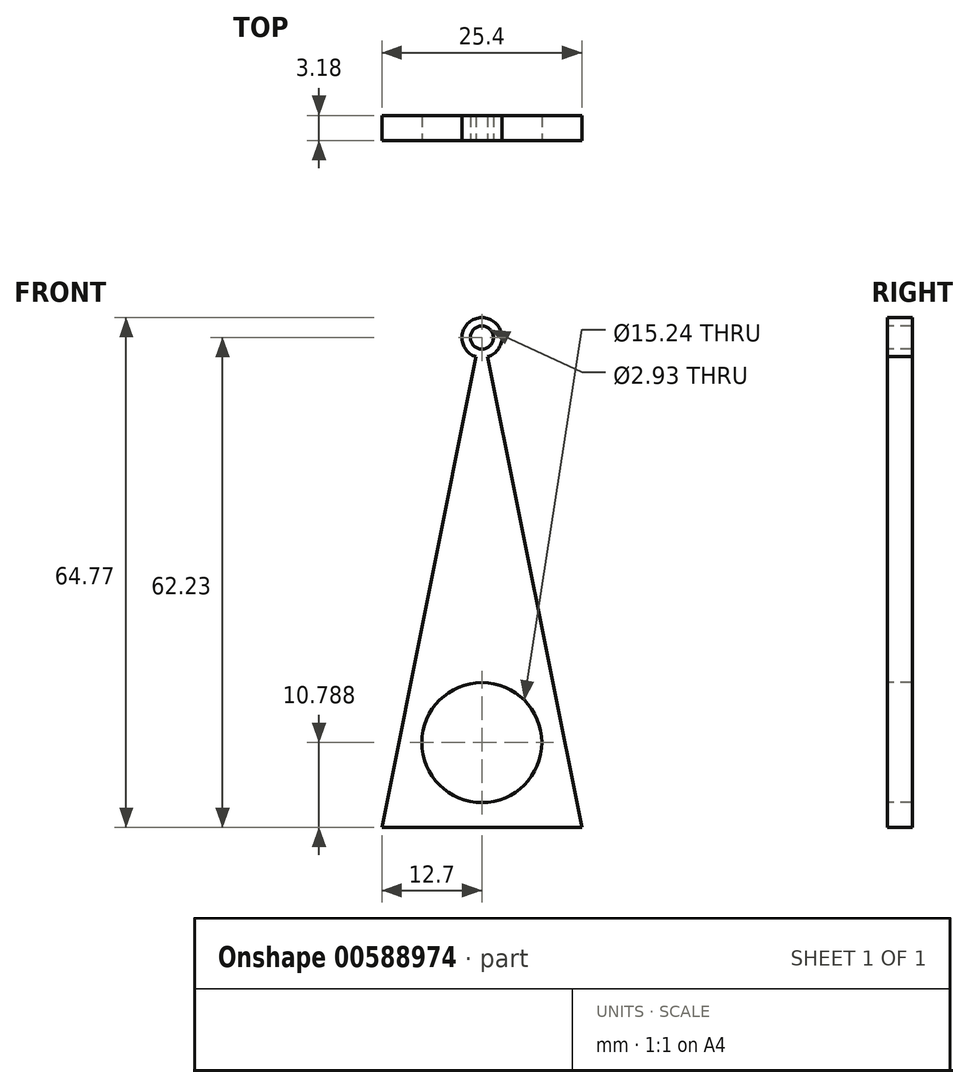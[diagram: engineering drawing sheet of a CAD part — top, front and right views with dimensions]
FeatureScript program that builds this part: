
annotation { "Feature Type Name" : "Feature", "Feature Type Description" : "" }
export const myFeature = defineFeature(function(context is Context, id is Id, definition is map)
    precondition{}
    {
        {
            var Q0;
            Q0=qCreatedBy(makeId("Front.planeOp"),FACE);
            var sketch = newSketch(context, id + "F0", { "sketchPlane" : qUnion([Q0])});
            skPoint(sketch, "E0", {"position": v(0, 38.1) * mm});
            skPoint(sketch, "E1", {"position": v(-12.7, -25.4) * mm});
            skPoint(sketch, "E2", {"position": v(12.7, -25.4) * mm});
            skLineSegment(sketch, "E3", {"start": v(0, 38.1) * mm, "end": v(-12.7, -25.4) * mm});
            skLineSegment(sketch, "E4", {"start": v(12.7, -25.4) * mm, "end": v(0, 38.1) * mm});
            skLineSegment(sketch, "E5", {"start": v(-12.7, -25.4) * mm, "end": v(12.7, -25.4) * mm});
            skSolve(sketch);
        }
        {
            var Q0;
            Q0 = qSketchRegion(id + "F0", true);
            extrude(context, id + "F1", {"entities" : qUnion([Q0]), "depth" : 3.17 * mm, "offsetDistance" : 25.4 * mm});
        }
        {
            var Q0;
            Q0=makeQuery(id+"F1.opExtrude","CAP_FACE",FACE,{"disambiguationData":[OSD([sQuery(id+"F0.wireOp",EDGE,"E3"),sQuery(id+"F0.wireOp",EDGE,"E4"),sQuery(id+"F0.wireOp",EDGE,"E5")])],"isStart":false});
            var sketch = newSketch(context, id + "F2", { "sketchPlane" : qUnion([Q0])});
            skCircle(sketch, "E6", {"center": v(0, -14.61) * mm, "radius": 7.62 * mm});
            skSolve(sketch);
        }
        {
            var Q0;
            Q0=makeQuery(id+"F2.imprint","IMPRINT",FACE,{"disambiguationData":[TD([[makeQuery(id+"F2.imprint","IMPRINT",EDGE,{"derivedFrom":sQuery(id+"F2.wireOp",EDGE,"E6")}),1.0]])]});
            extrude(context, id + "F3", {"entities" : qUnion([Q0]), "operationType" : NewBodyOperationType.REMOVE, "endBound" : BoundingType.THROUGH_ALL, "oppositeDirection" : true, "depth" : 25.4 * mm, "offsetDistance" : 25.4 * mm});
        }
        {
            var Q0;
            Q0=makeQuery(id+"F1.opExtrude","CAP_FACE",FACE,{"disambiguationData":[OSD([sQuery(id+"F0.wireOp",EDGE,"E3"),sQuery(id+"F0.wireOp",EDGE,"E4"),sQuery(id+"F0.wireOp",EDGE,"E5")])],"isStart":false});
            var sketch = newSketch(context, id + "F4", { "sketchPlane" : qUnion([Q0])});
            skCircle(sketch, "E7", {"center": v(0, 36.83) * mm, "radius": 2.54 * mm});
            skSolve(sketch);
        }
        {
            var Q0;
            {var subQ0=sQuery(id+"F4.wireOp",EDGE,"E7");var subQ1=makeQuery(id+"F1.opExtrude","CAP_EDGE",EDGE,{"disambiguationData":[OSD([sQuery(id+"F0.wireOp",EDGE,"E3")])],"isStart":false});var subQ2=makeQuery(id+"F4.imprint","INTERSECT",VERTEX,{"derivedFrom":[subQ1,subQ0]});Q0=makeQuery(id+"F4.imprint","IMPRINT",FACE,{"disambiguationData":[TD([[makeQuery(id+"F4.imprint","IMPRINT",EDGE,{"disambiguationData":[TD([[subQ2,1.0]])],"derivedFrom":subQ0}),1.0]])]});}
            var Q1;
            Q1=sQuery(id+"F4.wireOp",EDGE,"E7");
            var Q2;
            Q2=makeQuery(id+"F1.opExtrude","CAP_FACE",FACE,{"disambiguationData":[OSD([sQuery(id+"F0.wireOp",EDGE,"E3"),sQuery(id+"F0.wireOp",EDGE,"E4"),sQuery(id+"F0.wireOp",EDGE,"E5")])],"isStart":true});
            extrude(context, id + "F5", {"entities" : qUnion([Q0]), "operationType" : NewBodyOperationType.ADD, "surfaceEntities" : qUnion([Q1]), "endBound" : BoundingType.UP_TO_SURFACE, "oppositeDirection" : true, "depth" : 25.4 * mm, "endBoundEntityFace" : qUnion([Q2]), "offsetDistance" : 25.4 * mm});
        }
        {
            var Q0;
            {var subQ0=sQuery(id+"F0.wireOp",EDGE,"E4");var subQ1=sQuery(id+"F0.wireOp",EDGE,"E3");Q0=makeQuery(id+"F5.boolean.opBoolean","MERGE",FACE,{"derivedFrom":[makeQuery(id+"F1.opExtrude","CAP_FACE",FACE,{"disambiguationData":[OSD([subQ1,subQ0,sQuery(id+"F0.wireOp",EDGE,"E5")])],"isStart":false}),makeQuery(id+"F5.opExtrude","CAP_FACE",FACE,{"disambiguationData":[OSD([subQ1,subQ0,sQuery(id+"F4.wireOp",EDGE,"E7")])],"isStart":true})]});}
            var sketch = newSketch(context, id + "F6", { "sketchPlane" : qUnion([Q0])});
            skCircle(sketch, "E8", {"center": v(0, 36.83) * mm, "radius": 1.47 * mm});
            skSolve(sketch);
        }
        {
            var Q0;
            Q0=makeQuery(id+"F6.imprint","IMPRINT",FACE,{"disambiguationData":[TD([[makeQuery(id+"F6.imprint","IMPRINT",EDGE,{"derivedFrom":sQuery(id+"F6.wireOp",EDGE,"E8")}),1.0]])]});
            extrude(context, id + "F7", {"entities" : qUnion([Q0]), "operationType" : NewBodyOperationType.REMOVE, "endBound" : BoundingType.THROUGH_ALL, "oppositeDirection" : true, "depth" : 25.4 * mm, "offsetDistance" : 25.4 * mm});
        }
    });
